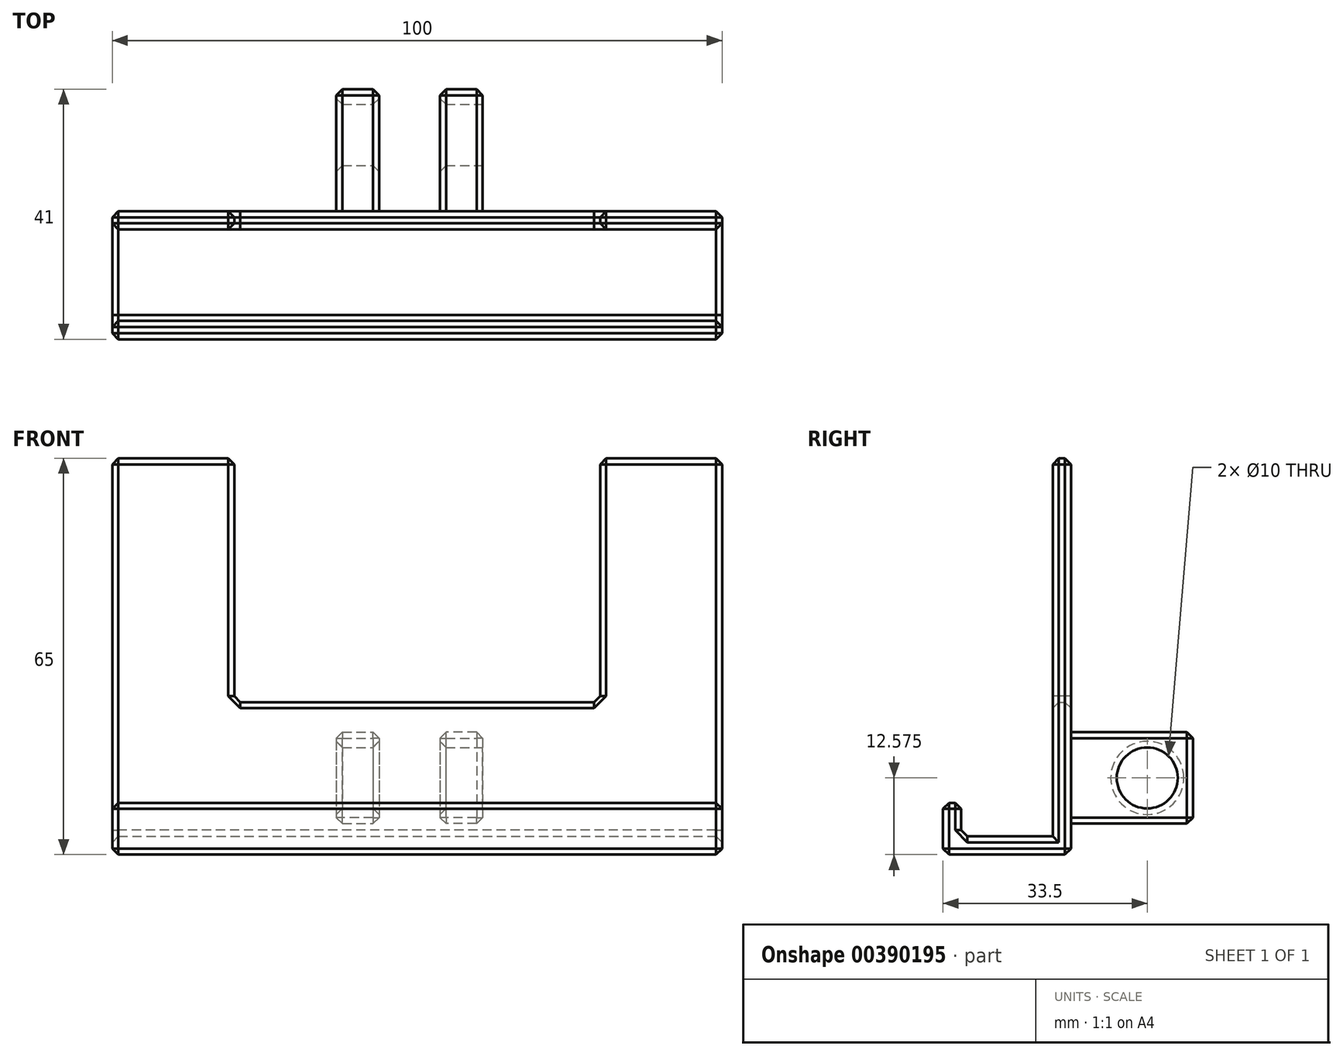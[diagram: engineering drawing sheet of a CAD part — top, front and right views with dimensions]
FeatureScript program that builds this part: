
annotation { "Feature Type Name" : "Feature", "Feature Type Description" : "" }
export const myFeature = defineFeature(function(context is Context, id is Id, definition is map)
    precondition{}
    {
        {
            var Q0;
            Q0=qCreatedBy(makeId("Front.planeOp"),FACE);
            var sketch = newSketch(context, id + "F0", { "sketchPlane" : qUnion([Q0])});
            skLineSegment(sketch, "E0", {"start": v(-48.74, 0) * mm, "end": v(51.26, 0) * mm});
            skLineSegment(sketch, "E1", {"start": v(51.26, 0) * mm, "end": v(51.26, 65) * mm});
            skLineSegment(sketch, "E2", {"start": v(51.26, 65) * mm, "end": v(31.26, 65) * mm});
            skLineSegment(sketch, "E3", {"start": v(31.26, 65) * mm, "end": v(31.26, 25) * mm});
            skLineSegment(sketch, "E4", {"start": v(31.26, 25) * mm, "end": v(-28.74, 25) * mm});
            skLineSegment(sketch, "E5", {"start": v(-28.74, 25) * mm, "end": v(-28.74, 65) * mm});
            skLineSegment(sketch, "E6", {"start": v(-28.74, 65) * mm, "end": v(-48.74, 65) * mm});
            skLineSegment(sketch, "E7", {"start": v(-48.74, 65) * mm, "end": v(-48.74, 0) * mm});
            skSolve(sketch);
        }
        {
            var Q0;
            Q0 = qSketchRegion(id + "F0", true);
            extrude(context, id + "F1", {"entities" : qUnion([Q0]), "depth" : 3 * mm});
        }
        {
            var Q0;
            Q0=makeQuery(id+"F1.opExtrude","SWEPT_FACE",FACE,{"disambiguationData":[OSD([sQuery(id+"F0.wireOp",EDGE,"E1")])]});
            var sketch = newSketch(context, id + "F2", { "sketchPlane" : qUnion([Q0])});
            skLineSegment(sketch, "E8", {"start": v(-1.5, 0) * mm, "end": v(-21, 0) * mm});
            skLineSegment(sketch, "E9", {"start": v(-21, 0) * mm, "end": v(-21, 8.5) * mm});
            skLineSegment(sketch, "E10", {"start": v(-21, 8.5) * mm, "end": v(-18, 8.5) * mm});
            skLineSegment(sketch, "E11", {"start": v(-18, 8.5) * mm, "end": v(-18, 3) * mm});
            skLineSegment(sketch, "E12", {"start": v(-18, 3) * mm, "end": v(-1.52, 3) * mm});
            skLineSegment(sketch, "E13", {"start": v(-1.52, 3) * mm, "end": v(-1.5, 0) * mm});
            skSolve(sketch);
        }
        {
            var Q0;
            {var subQ1=sQuery(id+"F2.wireOp",EDGE,"E9");Q0=makeQuery(id+"F2.imprint","IMPRINT",FACE,{"disambiguationData":[TD([[makeQuery(id+"F2.imprint","IMPRINT",EDGE,{"derivedFrom":subQ1}),-1.0]])]});}
            extrude(context, id + "F3", {"entities" : qUnion([Q0]), "operationType" : NewBodyOperationType.ADD, "oppositeDirection" : true, "depth" : 100 * mm});
        }
        {
            var Q0;
            Q0=makeQuery(id+"F1.opExtrude","CAP_FACE",FACE,{"disambiguationData":[OSD([sQuery(id+"F0.wireOp",EDGE,"E0"),sQuery(id+"F0.wireOp",EDGE,"E1"),sQuery(id+"F0.wireOp",EDGE,"E2"),sQuery(id+"F0.wireOp",EDGE,"E3"),sQuery(id+"F0.wireOp",EDGE,"E4"),sQuery(id+"F0.wireOp",EDGE,"E5"),sQuery(id+"F0.wireOp",EDGE,"E6"),sQuery(id+"F0.wireOp",EDGE,"E7")])],"isStart":true});
            var sketch = newSketch(context, id + "F4", { "sketchPlane" : qUnion([Q0])});
            skLineSegment(sketch, "E14.bottom", {"start": v(-12, 20.08) * mm, "end": v(-5, 20.08) * mm});
            skLineSegment(sketch, "E14.top", {"start": v(-12, 5.08) * mm, "end": v(-5, 5.08) * mm});
            skLineSegment(sketch, "E14.left", {"start": v(-12, 20.08) * mm, "end": v(-12, 5.08) * mm});
            skLineSegment(sketch, "E14.right", {"start": v(-5, 20.08) * mm, "end": v(-5, 5.08) * mm});
            skLineSegment(sketch, "E15.MirrorCS", {"start": v(5, 20.08) * mm, "end": v(5, 5.08) * mm});
            skLineSegment(sketch, "E16.MirrorCS", {"start": v(12, 20.08) * mm, "end": v(5, 20.08) * mm});
            skLineSegment(sketch, "E17.MirrorCS", {"start": v(12, 20.08) * mm, "end": v(12, 5.08) * mm});
            skLineSegment(sketch, "E18.MirrorCS", {"start": v(12, 5.08) * mm, "end": v(5, 5.08) * mm});
            skSolve(sketch);
        }
        {
            var Q0;
            Q0 = qSketchRegion(id + "F4", true);
            extrude(context, id + "F5", {"entities" : qUnion([Q0]), "operationType" : NewBodyOperationType.ADD, "depth" : 20 * mm});
        }
        {
            var Q0;
            Q0=makeQuery(id+"F5.opExtrude","SWEPT_FACE",FACE,{"disambiguationData":[OSD([sQuery(id+"F4.wireOp",EDGE,"E14.left")])]});
            var sketch = newSketch(context, id + "F6", { "sketchPlane" : qUnion([Q0])});
            skCircle(sketch, "E19", {"center": v(12.5, 12.58) * mm, "radius": 5 * mm});
            skSolve(sketch);
        }
        {
            var Q0;
            Q0 = qSketchRegion(id + "F6", true);
            extrude(context, id + "F7", {"entities" : qUnion([Q0]), "operationType" : NewBodyOperationType.REMOVE, "oppositeDirection" : true, "depth" : 25 * mm});
        }
        {
            var Q0;
            Q0=makeQuery(id+"F3.opExtrude","SWEPT_EDGE",EDGE,{"disambiguationData":[OSD([sQuery(id+"F0.wireOp",EDGE,"E1"),sQuery(id+"F2.wireOp",EDGE,"E12")])]});
            var Q1;
            Q1=makeQuery(id+"F3.opExtrude","SWEPT_EDGE",EDGE,{"disambiguationData":[OSD([sQuery(id+"F2.wireOp",EDGE,"E11"),sQuery(id+"F2.wireOp",EDGE,"E12")])]});
            var Q2;
            Q2=makeQuery(id+"F5.opExtrude","CAP_EDGE",EDGE,{"disambiguationData":[OSD([sQuery(id+"F4.wireOp",EDGE,"E14.left")])],"isStart":true});
            var Q3;
            Q3=makeQuery(id+"F5.opExtrude","CAP_EDGE",EDGE,{"disambiguationData":[OSD([sQuery(id+"F4.wireOp",EDGE,"E14.bottom")])],"isStart":true});
            var Q4;
            Q4=makeQuery(id+"F5.opExtrude","CAP_EDGE",EDGE,{"disambiguationData":[OSD([sQuery(id+"F4.wireOp",EDGE,"E14.right")])],"isStart":true});
            var Q5;
            Q5=makeQuery(id+"F5.opExtrude","CAP_EDGE",EDGE,{"disambiguationData":[OSD([sQuery(id+"F4.wireOp",EDGE,"E14.top")])],"isStart":true});
            var Q6;
            Q6=makeQuery(id+"F5.opExtrude","CAP_EDGE",EDGE,{"disambiguationData":[OSD([sQuery(id+"F4.wireOp",EDGE,"E18.MirrorCS")])],"isStart":true});
            var Q7;
            Q7=makeQuery(id+"F5.opExtrude","CAP_EDGE",EDGE,{"disambiguationData":[OSD([sQuery(id+"F4.wireOp",EDGE,"E17.MirrorCS")])],"isStart":true});
            var Q8;
            Q8=makeQuery(id+"F5.opExtrude","CAP_EDGE",EDGE,{"disambiguationData":[OSD([sQuery(id+"F4.wireOp",EDGE,"E16.MirrorCS")])],"isStart":true});
            var Q9;
            Q9=makeQuery(id+"F5.opExtrude","CAP_EDGE",EDGE,{"disambiguationData":[OSD([sQuery(id+"F4.wireOp",EDGE,"E15.MirrorCS")])],"isStart":true});
            var Q10;
            Q10=makeQuery(id+"F7.boolean.opBoolean","COPY",EDGE,{"derivedFrom":makeQuery(id+"F7.opExtrude","CAP_EDGE",EDGE,{"disambiguationData":[OSD([sQuery(id+"F6.wireOp",EDGE,"E19")])],"isStart":true})});
            var Q11;
            Q11=makeQuery(id+"F7.boolean.opBoolean","INTERSECT",EDGE,{"derivedFrom":[makeQuery(id+"F5.opExtrude","SWEPT_FACE",FACE,{"disambiguationData":[OSD([sQuery(id+"F4.wireOp",EDGE,"E14.right")])]}),makeQuery(id+"F7.opExtrude","SWEPT_FACE",FACE,{"disambiguationData":[OSD([sQuery(id+"F6.wireOp",EDGE,"E19")])]})]});
            var Q12;
            Q12=makeQuery(id+"F7.boolean.opBoolean","INTERSECT",EDGE,{"derivedFrom":[makeQuery(id+"F5.opExtrude","SWEPT_FACE",FACE,{"disambiguationData":[OSD([sQuery(id+"F4.wireOp",EDGE,"E17.MirrorCS")])]}),makeQuery(id+"F7.opExtrude","SWEPT_FACE",FACE,{"disambiguationData":[OSD([sQuery(id+"F6.wireOp",EDGE,"E19")])]})]});
            var Q13;
            Q13=makeQuery(id+"F7.boolean.opBoolean","INTERSECT",EDGE,{"derivedFrom":[makeQuery(id+"F5.opExtrude","SWEPT_FACE",FACE,{"disambiguationData":[OSD([sQuery(id+"F4.wireOp",EDGE,"E15.MirrorCS")])]}),makeQuery(id+"F7.opExtrude","SWEPT_FACE",FACE,{"disambiguationData":[OSD([sQuery(id+"F6.wireOp",EDGE,"E19")])]})]});
            var Q14;
            Q14=makeQuery(id+"F3.boolean.opBoolean","MERGE",EDGE,{"derivedFrom":[makeQuery(id+"F1.opExtrude","SWEPT_EDGE",EDGE,{"disambiguationData":[OSD([sQuery(id+"F0.wireOp",EDGE,"E0"),sQuery(id+"F0.wireOp",EDGE,"E1")])]}),makeQuery(id+"F3.opExtrude","CAP_EDGE",EDGE,{"disambiguationData":[OSD([sQuery(id+"F2.wireOp",EDGE,"E8")])],"isStart":true})]});
            var Q15;
            Q15=makeQuery(id+"F3.opExtrude","SWEPT_EDGE",EDGE,{"disambiguationData":[OSD([sQuery(id+"F2.wireOp",EDGE,"E8"),sQuery(id+"F2.wireOp",EDGE,"E9")])]});
            var Q16;
            Q16=makeQuery(id+"F1.opExtrude","CAP_EDGE",EDGE,{"disambiguationData":[OSD([sQuery(id+"F0.wireOp",EDGE,"E0")])],"isStart":true});
            var Q17;
            Q17=makeQuery(id+"F3.boolean.opBoolean","MERGE",EDGE,{"derivedFrom":[makeQuery(id+"F1.opExtrude","SWEPT_EDGE",EDGE,{"disambiguationData":[OSD([sQuery(id+"F0.wireOp",EDGE,"E0"),sQuery(id+"F0.wireOp",EDGE,"E7")])]}),makeQuery(id+"F3.opExtrude","CAP_EDGE",EDGE,{"disambiguationData":[OSD([sQuery(id+"F2.wireOp",EDGE,"E8")])],"isStart":false})]});
            var Q18;
            Q18=makeQuery(id+"F3.opExtrude","SWEPT_EDGE",EDGE,{"disambiguationData":[OSD([sQuery(id+"F2.wireOp",EDGE,"E9"),sQuery(id+"F2.wireOp",EDGE,"E10")])]});
            var Q19;
            Q19=makeQuery(id+"F3.opExtrude","SWEPT_EDGE",EDGE,{"disambiguationData":[OSD([sQuery(id+"F2.wireOp",EDGE,"E10"),sQuery(id+"F2.wireOp",EDGE,"E11")])]});
            var Q20;
            Q20=makeQuery(id+"F3.opExtrude","CAP_EDGE",EDGE,{"disambiguationData":[OSD([sQuery(id+"F2.wireOp",EDGE,"E10")])],"isStart":false});
            var Q21;
            Q21=makeQuery(id+"F3.opExtrude","CAP_EDGE",EDGE,{"disambiguationData":[OSD([sQuery(id+"F2.wireOp",EDGE,"E10")])],"isStart":true});
            var Q22;
            Q22=makeQuery(id+"F1.opExtrude","CAP_EDGE",EDGE,{"disambiguationData":[OSD([sQuery(id+"F0.wireOp",EDGE,"E4")])],"isStart":false});
            var Q23;
            Q23=makeQuery(id+"F1.opExtrude","CAP_EDGE",EDGE,{"disambiguationData":[OSD([sQuery(id+"F0.wireOp",EDGE,"E3")])],"isStart":false});
            var Q24;
            Q24=makeQuery(id+"F1.opExtrude","CAP_EDGE",EDGE,{"disambiguationData":[OSD([sQuery(id+"F0.wireOp",EDGE,"E2")])],"isStart":false});
            var Q25;
            Q25=makeQuery(id+"F1.opExtrude","CAP_EDGE",EDGE,{"disambiguationData":[OSD([sQuery(id+"F0.wireOp",EDGE,"E1")])],"isStart":false});
            var Q26;
            Q26=makeQuery(id+"F1.opExtrude","CAP_EDGE",EDGE,{"disambiguationData":[OSD([sQuery(id+"F0.wireOp",EDGE,"E7")])],"isStart":false});
            var Q27;
            Q27=makeQuery(id+"F1.opExtrude","CAP_EDGE",EDGE,{"disambiguationData":[OSD([sQuery(id+"F0.wireOp",EDGE,"E7")])],"isStart":true});
            var Q28;
            Q28=makeQuery(id+"F1.opExtrude","CAP_EDGE",EDGE,{"disambiguationData":[OSD([sQuery(id+"F0.wireOp",EDGE,"E5")])],"isStart":false});
            var Q29;
            Q29=makeQuery(id+"F1.opExtrude","CAP_EDGE",EDGE,{"disambiguationData":[OSD([sQuery(id+"F0.wireOp",EDGE,"E6")])],"isStart":false});
            var Q30;
            Q30=makeQuery(id+"F1.opExtrude","CAP_EDGE",EDGE,{"disambiguationData":[OSD([sQuery(id+"F0.wireOp",EDGE,"E5")])],"isStart":true});
            var Q31;
            Q31=makeQuery(id+"F1.opExtrude","CAP_EDGE",EDGE,{"disambiguationData":[OSD([sQuery(id+"F0.wireOp",EDGE,"E4")])],"isStart":true});
            var Q32;
            Q32=makeQuery(id+"F1.opExtrude","CAP_EDGE",EDGE,{"disambiguationData":[OSD([sQuery(id+"F0.wireOp",EDGE,"E3")])],"isStart":true});
            var Q33;
            Q33=makeQuery(id+"F1.opExtrude","SWEPT_EDGE",EDGE,{"disambiguationData":[OSD([sQuery(id+"F0.wireOp",EDGE,"E2"),sQuery(id+"F0.wireOp",EDGE,"E3")])]});
            var Q34;
            Q34=makeQuery(id+"F1.opExtrude","SWEPT_EDGE",EDGE,{"disambiguationData":[OSD([sQuery(id+"F0.wireOp",EDGE,"E3"),sQuery(id+"F0.wireOp",EDGE,"E4")])]});
            var Q35;
            Q35=makeQuery(id+"F1.opExtrude","SWEPT_EDGE",EDGE,{"disambiguationData":[OSD([sQuery(id+"F0.wireOp",EDGE,"E5"),sQuery(id+"F0.wireOp",EDGE,"E6")])]});
            var Q36;
            Q36=makeQuery(id+"F1.opExtrude","CAP_EDGE",EDGE,{"disambiguationData":[OSD([sQuery(id+"F0.wireOp",EDGE,"E1")])],"isStart":true});
            var Q37;
            Q37=makeQuery(id+"F1.opExtrude","CAP_EDGE",EDGE,{"disambiguationData":[OSD([sQuery(id+"F0.wireOp",EDGE,"E2")])],"isStart":true});
            var Q38;
            Q38=makeQuery(id+"F3.opExtrude","CAP_EDGE",EDGE,{"disambiguationData":[OSD([sQuery(id+"F2.wireOp",EDGE,"E12")])],"isStart":false});
            var Q39;
            Q39=makeQuery(id+"F1.opExtrude","CAP_EDGE",EDGE,{"disambiguationData":[OSD([sQuery(id+"F0.wireOp",EDGE,"E6")])],"isStart":true});
            var Q40;
            Q40=makeQuery(id+"F5.opExtrude","SWEPT_EDGE",EDGE,{"disambiguationData":[OSD([sQuery(id+"F4.wireOp",EDGE,"E14.bottom"),sQuery(id+"F4.wireOp",EDGE,"E14.left")])]});
            var Q41;
            Q41=makeQuery(id+"F5.opExtrude","SWEPT_EDGE",EDGE,{"disambiguationData":[OSD([sQuery(id+"F4.wireOp",EDGE,"E14.bottom"),sQuery(id+"F4.wireOp",EDGE,"E14.right")])]});
            var Q42;
            Q42=makeQuery(id+"F5.opExtrude","SWEPT_EDGE",EDGE,{"disambiguationData":[OSD([sQuery(id+"F4.wireOp",EDGE,"E14.top"),sQuery(id+"F4.wireOp",EDGE,"E14.right")])]});
            var Q43;
            Q43=makeQuery(id+"F5.opExtrude","SWEPT_EDGE",EDGE,{"disambiguationData":[OSD([sQuery(id+"F4.wireOp",EDGE,"E15.MirrorCS"),sQuery(id+"F4.wireOp",EDGE,"E16.MirrorCS")])]});
            var Q44;
            Q44=makeQuery(id+"F5.opExtrude","SWEPT_EDGE",EDGE,{"disambiguationData":[OSD([sQuery(id+"F4.wireOp",EDGE,"E16.MirrorCS"),sQuery(id+"F4.wireOp",EDGE,"E17.MirrorCS")])]});
            var Q45;
            Q45=makeQuery(id+"F5.opExtrude","SWEPT_EDGE",EDGE,{"disambiguationData":[OSD([sQuery(id+"F4.wireOp",EDGE,"E17.MirrorCS"),sQuery(id+"F4.wireOp",EDGE,"E18.MirrorCS")])]});
            var Q46;
            Q46=makeQuery(id+"F5.opExtrude","CAP_EDGE",EDGE,{"disambiguationData":[OSD([sQuery(id+"F4.wireOp",EDGE,"E14.bottom")])],"isStart":false});
            var Q47;
            Q47=makeQuery(id+"F5.opExtrude","CAP_EDGE",EDGE,{"disambiguationData":[OSD([sQuery(id+"F4.wireOp",EDGE,"E14.top")])],"isStart":false});
            var Q48;
            Q48=makeQuery(id+"F5.opExtrude","CAP_EDGE",EDGE,{"disambiguationData":[OSD([sQuery(id+"F4.wireOp",EDGE,"E15.MirrorCS")])],"isStart":false});
            var Q49;
            Q49=makeQuery(id+"F5.opExtrude","CAP_EDGE",EDGE,{"disambiguationData":[OSD([sQuery(id+"F4.wireOp",EDGE,"E16.MirrorCS")])],"isStart":false});
            var Q50;
            Q50=makeQuery(id+"F5.opExtrude","CAP_EDGE",EDGE,{"disambiguationData":[OSD([sQuery(id+"F4.wireOp",EDGE,"E17.MirrorCS")])],"isStart":false});
            var Q51;
            Q51=makeQuery(id+"F1.opExtrude","SWEPT_EDGE",EDGE,{"disambiguationData":[OSD([sQuery(id+"F0.wireOp",EDGE,"E1"),sQuery(id+"F0.wireOp",EDGE,"E2")])]});
            var Q52;
            Q52=makeQuery(id+"F1.opExtrude","SWEPT_EDGE",EDGE,{"disambiguationData":[OSD([sQuery(id+"F0.wireOp",EDGE,"E4"),sQuery(id+"F0.wireOp",EDGE,"E5")])]});
            var Q53;
            Q53=makeQuery(id+"F1.opExtrude","SWEPT_EDGE",EDGE,{"disambiguationData":[OSD([sQuery(id+"F0.wireOp",EDGE,"E6"),sQuery(id+"F0.wireOp",EDGE,"E7")])]});
            var Q54;
            Q54=makeQuery(id+"F3.opExtrude","CAP_EDGE",EDGE,{"disambiguationData":[OSD([sQuery(id+"F2.wireOp",EDGE,"E11")])],"isStart":false});
            var Q55;
            Q55=makeQuery(id+"F3.opExtrude","CAP_EDGE",EDGE,{"disambiguationData":[OSD([sQuery(id+"F2.wireOp",EDGE,"E12")])],"isStart":true});
            var Q56;
            Q56=makeQuery(id+"F3.opExtrude","CAP_EDGE",EDGE,{"disambiguationData":[OSD([sQuery(id+"F2.wireOp",EDGE,"E9")])],"isStart":true});
            var Q57;
            Q57=makeQuery(id+"F3.opExtrude","CAP_EDGE",EDGE,{"disambiguationData":[OSD([sQuery(id+"F2.wireOp",EDGE,"E9")])],"isStart":false});
            var Q58;
            Q58=makeQuery(id+"F3.opExtrude","CAP_EDGE",EDGE,{"disambiguationData":[OSD([sQuery(id+"F2.wireOp",EDGE,"E11")])],"isStart":true});
            var Q59;
            Q59=makeQuery(id+"F5.opExtrude","CAP_EDGE",EDGE,{"disambiguationData":[OSD([sQuery(id+"F4.wireOp",EDGE,"E14.left")])],"isStart":false});
            var Q60;
            Q60=makeQuery(id+"F5.opExtrude","CAP_EDGE",EDGE,{"disambiguationData":[OSD([sQuery(id+"F4.wireOp",EDGE,"E14.right")])],"isStart":false});
            var Q61;
            Q61=makeQuery(id+"F5.opExtrude","SWEPT_EDGE",EDGE,{"disambiguationData":[OSD([sQuery(id+"F4.wireOp",EDGE,"E14.top"),sQuery(id+"F4.wireOp",EDGE,"E14.left")])]});
            var Q62;
            Q62=makeQuery(id+"F5.opExtrude","SWEPT_EDGE",EDGE,{"disambiguationData":[OSD([sQuery(id+"F4.wireOp",EDGE,"E15.MirrorCS"),sQuery(id+"F4.wireOp",EDGE,"E18.MirrorCS")])]});
            var Q63;
            Q63=makeQuery(id+"F5.opExtrude","CAP_EDGE",EDGE,{"disambiguationData":[OSD([sQuery(id+"F4.wireOp",EDGE,"E18.MirrorCS")])],"isStart":false});
            chamfer(context, id + "F8", {"entities" : qUnion([Q0, Q1, Q2, Q3, Q4, Q5, Q6, Q7, Q8, Q9, Q10, Q11, Q12, Q13, Q14, Q15, Q16, Q17, Q18, Q19, Q20, Q21, Q22, Q23, Q24, Q25, Q26, Q27, Q28, Q29, Q30, Q31, Q32, Q33, Q34, Q35, Q36, Q37, Q38, Q39, Q40, Q41, Q42, Q43, Q44, Q45, Q46, Q47, Q48, Q49, Q50, Q51, Q52, Q53, Q54, Q55, Q56, Q57, Q58, Q59, Q60, Q61, Q62, Q63]), "width" : 1 * mm, "tangentPropagation" : true});
        }
    });
